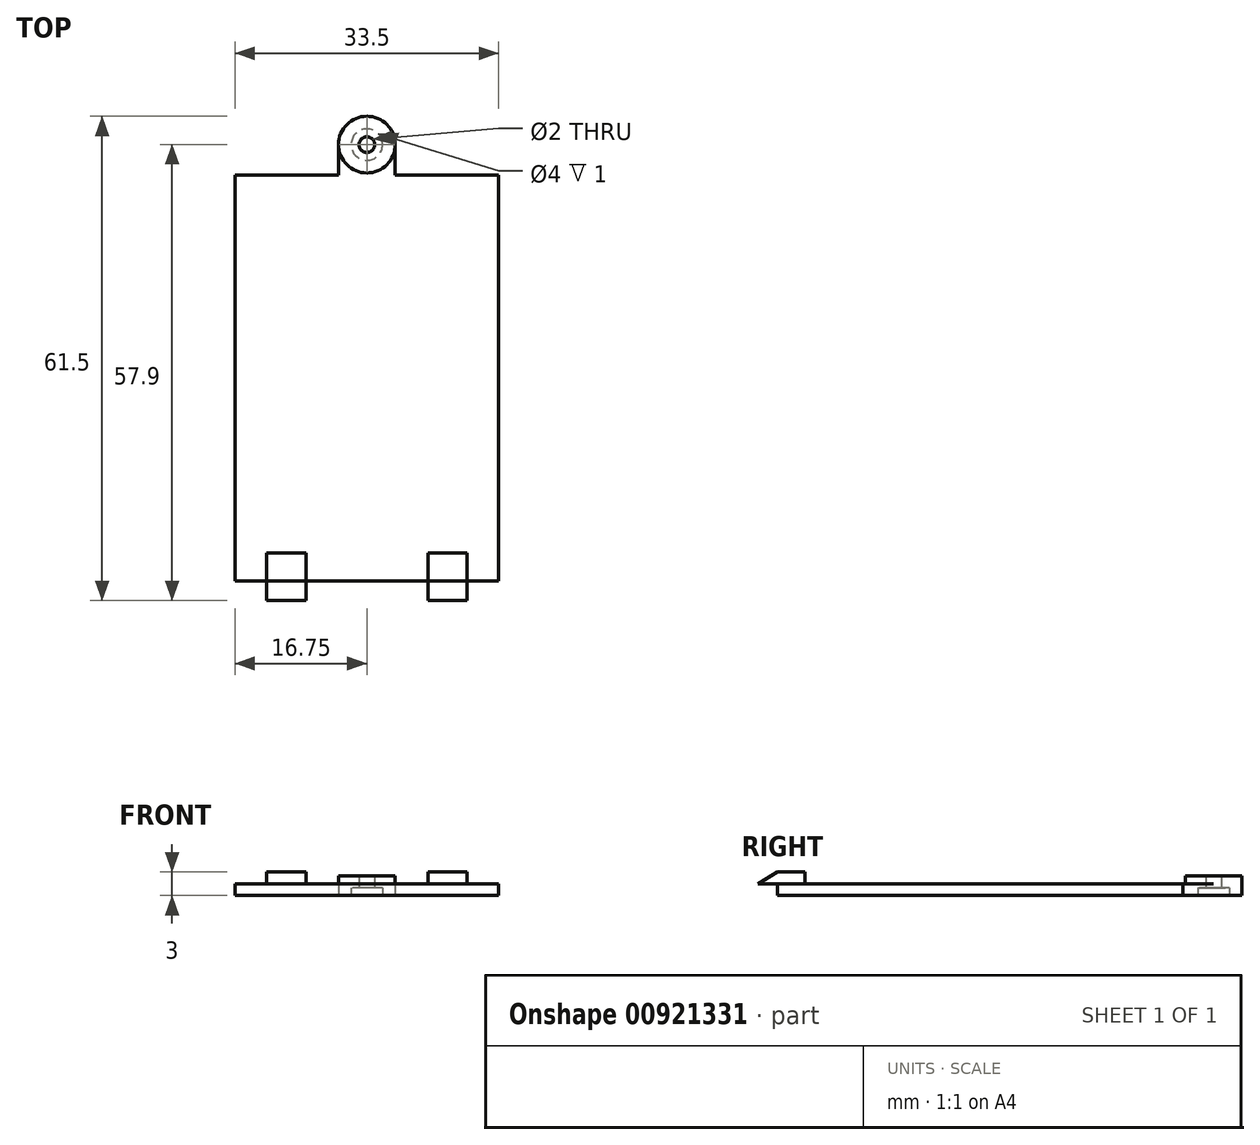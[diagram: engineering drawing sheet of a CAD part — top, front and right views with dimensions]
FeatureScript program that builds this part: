
annotation { "Feature Type Name" : "Feature", "Feature Type Description" : "" }
export const myFeature = defineFeature(function(context is Context, id is Id, definition is map)
    precondition{}
    {
        {
            var Q0;
            Q0=qCreatedBy(makeId("Top.planeOp"),FACE);
            var sketch = newSketch(context, id + "F0", { "sketchPlane" : qUnion([Q0])});
            skLineSegment(sketch, "E0", {"start": v(0, 0) * mm, "end": v(-16.75, 0) * mm});
            skLineSegment(sketch, "E1", {"start": v(0, 0) * mm, "end": v(16.75, 0) * mm});
            skLineSegment(sketch, "E2", {"start": v(16.75, 0) * mm, "end": v(16.75, 51.5) * mm});
            skLineSegment(sketch, "E3", {"start": v(16.75, 51.5) * mm, "end": v(-16.75, 51.5) * mm});
            skLineSegment(sketch, "E4", {"start": v(-16.75, 51.5) * mm, "end": v(-16.75, 0) * mm});
            skLineSegment(sketch, "E5", {"start": v(0, 51.5) * mm, "end": v(-3.6, 51.5) * mm});
            skCircle(sketch, "E6", {"center": v(0, 55.4) * mm, "radius": 3.6 * mm});
            skLineSegment(sketch, "E7", {"start": v(-3.6, 55.4) * mm, "end": v(-3.6, 51.5) * mm});
            skLineSegment(sketch, "E8", {"start": v(3.6, 55.4) * mm, "end": v(3.6, 51.5) * mm});
            skCircle(sketch, "E9", {"center": v(0, 55.4) * mm, "radius": 1 * mm});
            skCircle(sketch, "E10", {"center": v(0, 55.4) * mm, "radius": 2 * mm});
            skSolve(sketch);
        }
        {
            var Q0;
            Q0=makeQuery(id+"F0.imprint","IMPRINT",FACE,{"disambiguationData":[TD([[makeQuery(id+"F0.imprint","IMPRINT",EDGE,{"derivedFrom":sQuery(id+"F0.wireOp",EDGE,"E0")}),-1.0]])]});
            var Q1;
            {var subQ0=sQuery(id+"F0.wireOp",EDGE,"E5");Q1=makeQuery(id+"F0.imprint","IMPRINT",FACE,{"disambiguationData":[TD([[makeQuery(id+"F0.imprint","IMPRINT",EDGE,{"derivedFrom":subQ0}),-1.0]])]});}
            var Q2;
            {var subQ3=sQuery(id+"F0.wireOp",EDGE,"E8");Q2=makeQuery(id+"F0.imprint","IMPRINT",FACE,{"disambiguationData":[TD([[makeQuery(id+"F0.imprint","IMPRINT",EDGE,{"derivedFrom":subQ3}),-1.0]])]});}
            var Q3;
            {var subQ0=sQuery(id+"F0.wireOp",EDGE,"Crr1LPVL-UAtX-yI9U-8Ite-RvZtyMZe4BYH");Q3=makeQuery(id+"F0.imprint","IMPRINT",FACE,{"disambiguationData":[TD([[makeQuery(id+"F0.imprint","IMPRINT",EDGE,{"derivedFrom":subQ0}),-1.0]])]});}
            var Q4;
            {var subQ0=sQuery(id+"F0.wireOp",EDGE,"1Us7f2dU-Pjqd-qusr-gRFw-1HQ45FjS2ouL");Q4=makeQuery(id+"F0.imprint","IMPRINT",FACE,{"disambiguationData":[TD([[makeQuery(id+"F0.imprint","IMPRINT",EDGE,{"derivedFrom":subQ0}),1.0]])]});}
            var Q5;
            {var subQ0=sQuery(id+"F0.wireOp",EDGE,"3M23ZBgI-908c-eMXX-ZKFW-ISIKOpE3Sat9");Q5=makeQuery(id+"F0.imprint","IMPRINT",FACE,{"disambiguationData":[TD([[makeQuery(id+"F0.imprint","IMPRINT",EDGE,{"derivedFrom":subQ0}),-1.0]])]});}
            var Q6;
            {var subQ0=sQuery(id+"F0.wireOp",EDGE,"3M23ZBgI-908c-eMXX-ZKFW-ISIKOpE3Sat9");Q6=makeQuery(id+"F0.imprint","IMPRINT",FACE,{"disambiguationData":[TD([[makeQuery(id+"F0.imprint","IMPRINT",EDGE,{"derivedFrom":subQ0}),1.0]])]});}
            var Q7;
            Q7=makeQuery(id+"F0.imprint","IMPRINT",FACE,{"disambiguationData":[TD([[makeQuery(id+"F0.imprint","IMPRINT",EDGE,{"derivedFrom":sQuery(id+"F0.wireOp",EDGE,"E9")}),-1.0]])]});
            var Q8;
            Q8=makeQuery(id+"F0.imprint","IMPRINT",FACE,{"disambiguationData":[TD([[makeQuery(id+"F0.imprint","IMPRINT",EDGE,{"derivedFrom":sQuery(id+"F0.wireOp",EDGE,"E9")}),1.0]])]});
            var Q9;
            Q9=makeQuery(id+"F0.imprint","IMPRINT",FACE,{"disambiguationData":[TD([[makeQuery(id+"F0.imprint","IMPRINT",EDGE,{"derivedFrom":sQuery(id+"F0.wireOp",EDGE,"E10")}),-1.0]])]});
            extrude(context, id + "F1", {"entities" : qUnion([Q0, Q1, Q2, Q3, Q4, Q5, Q6, Q7, Q8, Q9]), "depth" : 1.5 * mm, "offsetDistance" : 25 * mm});
        }
        {
            var Q0;
            {var subQ0=sQuery(id+"F0.wireOp",EDGE,"Crr1LPVL-UAtX-yI9U-8Ite-RvZtyMZe4BYH");Q0=makeQuery(id+"F0.imprint","IMPRINT",FACE,{"disambiguationData":[TD([[makeQuery(id+"F0.imprint","IMPRINT",EDGE,{"derivedFrom":subQ0}),-1.0]])]});}
            var Q1;
            {var subQ0=sQuery(id+"F0.wireOp",EDGE,"1Us7f2dU-Pjqd-qusr-gRFw-1HQ45FjS2ouL");Q1=makeQuery(id+"F0.imprint","IMPRINT",FACE,{"disambiguationData":[TD([[makeQuery(id+"F0.imprint","IMPRINT",EDGE,{"derivedFrom":subQ0}),1.0]])]});}
            var Q2;
            {var subQ0=sQuery(id+"F0.wireOp",EDGE,"3M23ZBgI-908c-eMXX-ZKFW-ISIKOpE3Sat9");Q2=makeQuery(id+"F0.imprint","IMPRINT",FACE,{"disambiguationData":[TD([[makeQuery(id+"F0.imprint","IMPRINT",EDGE,{"derivedFrom":subQ0}),-1.0]])]});}
            var Q3;
            {var subQ0=sQuery(id+"F0.wireOp",EDGE,"3M23ZBgI-908c-eMXX-ZKFW-ISIKOpE3Sat9");Q3=makeQuery(id+"F0.imprint","IMPRINT",FACE,{"disambiguationData":[TD([[makeQuery(id+"F0.imprint","IMPRINT",EDGE,{"derivedFrom":subQ0}),1.0]])]});}
            var Q4;
            {var subQ0=sQuery(id+"F0.wireOp",EDGE,"E6");var subQ1=makeQuery(id+"F0.imprint","INTERSECT",VERTEX,{"derivedFrom":[subQ0,sQuery(id+"F0.wireOp",EDGE,"E7")]});Q4=makeQuery(id+"F0.imprint","IMPRINT",FACE,{"disambiguationData":[TD([[makeQuery(id+"F0.imprint","IMPRINT",EDGE,{"disambiguationData":[TD([[subQ1,1.0]])],"derivedFrom":subQ0}),1.0]])]});}
            var Q5;
            Q5=makeQuery(id+"F0.imprint","IMPRINT",FACE,{"disambiguationData":[TD([[makeQuery(id+"F0.imprint","IMPRINT",EDGE,{"derivedFrom":sQuery(id+"F0.wireOp",EDGE,"E9")}),-1.0]])]});
            var Q6;
            Q6=makeQuery(id+"F0.imprint","IMPRINT",FACE,{"disambiguationData":[TD([[makeQuery(id+"F0.imprint","IMPRINT",EDGE,{"derivedFrom":sQuery(id+"F0.wireOp",EDGE,"E9")}),1.0]])]});
            extrude(context, id + "F2", {"entities" : qUnion([Q0, Q1, Q2, Q3, Q4, Q5, Q6]), "operationType" : NewBodyOperationType.ADD, "depth" : 2.5 * mm, "offsetDistance" : 25 * mm});
        }
        {
            var Q0;
            Q0=makeQuery(id+"F1.opExtrude","CAP_FACE",FACE,{"disambiguationData":[OSD([sQuery(id+"F0.wireOp",EDGE,"E0"),sQuery(id+"F0.wireOp",EDGE,"E1"),sQuery(id+"F0.wireOp",EDGE,"E2"),sQuery(id+"F0.wireOp",EDGE,"E3"),sQuery(id+"F0.wireOp",EDGE,"E4"),sQuery(id+"F0.wireOp",EDGE,"E6"),sQuery(id+"F0.wireOp",EDGE,"E7"),sQuery(id+"F0.wireOp",EDGE,"E8")])],"isStart":false});
            var sketch = newSketch(context, id + "F3", { "sketchPlane" : qUnion([Q0])});
            skLineSegment(sketch, "E11", {"start": v(12.74, 0) * mm, "end": v(12.74, 3.5) * mm});
            skLineSegment(sketch, "E12", {"start": v(12.74, 3.5) * mm, "end": v(7.74, 3.5) * mm});
            skLineSegment(sketch, "E13", {"start": v(7.74, 3.5) * mm, "end": v(7.74, -2.5) * mm});
            skLineSegment(sketch, "E14", {"start": v(7.74, -2.5) * mm, "end": v(12.74, -2.5) * mm});
            skLineSegment(sketch, "E15", {"start": v(12.74, -2.5) * mm, "end": v(12.74, 0) * mm});
            skLineSegment(sketch, "E16", {"start": v(0, 0.9) * mm, "end": v(0, 19.62) * mm});
            skLineSegment(sketch, "E17.MirrorCS", {"start": v(-12.74, 3.5) * mm, "end": v(-7.74, 3.5) * mm});
            skLineSegment(sketch, "E18.MirrorCS", {"start": v(-12.74, 0) * mm, "end": v(-12.74, 3.5) * mm});
            skLineSegment(sketch, "E19.MirrorCS", {"start": v(-12.74, -2.5) * mm, "end": v(-12.74, 0) * mm});
            skLineSegment(sketch, "E20.MirrorCS", {"start": v(-7.74, -2.5) * mm, "end": v(-12.74, -2.5) * mm});
            skLineSegment(sketch, "E21.MirrorCS", {"start": v(-7.74, 3.5) * mm, "end": v(-7.74, -2.5) * mm});
            skSolve(sketch);
        }
        {
            var Q0;
            {var subQ0=sQuery(id+"F3.wireOp",EDGE,"E19.MirrorCS");Q0=makeQuery(id+"F3.imprint","IMPRINT",FACE,{"disambiguationData":[TD([[makeQuery(id+"F3.imprint","IMPRINT",EDGE,{"derivedFrom":subQ0}),-1.0]])]});}
            var Q1;
            {var subQ0=sQuery(id+"F3.wireOp",EDGE,"E17.MirrorCS");Q1=makeQuery(id+"F3.imprint","IMPRINT",FACE,{"disambiguationData":[TD([[makeQuery(id+"F3.imprint","IMPRINT",EDGE,{"derivedFrom":subQ0}),-1.0]])]});}
            var Q2;
            {var subQ0=sQuery(id+"F3.wireOp",EDGE,"E14");Q2=makeQuery(id+"F3.imprint","IMPRINT",FACE,{"disambiguationData":[TD([[makeQuery(id+"F3.imprint","IMPRINT",EDGE,{"derivedFrom":subQ0}),1.0]])]});}
            var Q3;
            {var subQ0=sQuery(id+"F3.wireOp",EDGE,"E11");Q3=makeQuery(id+"F3.imprint","IMPRINT",FACE,{"disambiguationData":[TD([[makeQuery(id+"F3.imprint","IMPRINT",EDGE,{"derivedFrom":subQ0}),1.0]])]});}
            extrude(context, id + "F4", {"entities" : qUnion([Q0, Q1, Q2, Q3]), "operationType" : NewBodyOperationType.ADD, "depth" : 1.5 * mm, "offsetDistance" : 25 * mm});
        }
        {
            var Q0;
            Q0=makeQuery(id+"F4.opExtrude","CAP_EDGE",EDGE,{"disambiguationData":[OSD([sQuery(id+"F3.wireOp",EDGE,"E20.MirrorCS")])],"isStart":false});
            chamfer(context, id + "F5", {"entities" : qUnion([Q0]), "chamferType" : ChamferType.TWO_OFFSETS, "width1" : 1.5 * mm, "oppositeDirection" : false, "width2" : 2.5 * mm, "tangentPropagation" : true});
        }
        {
            var Q0;
            Q0=makeQuery(id+"F4.opExtrude","CAP_EDGE",EDGE,{"disambiguationData":[OSD([sQuery(id+"F3.wireOp",EDGE,"E14")])],"isStart":false});
            chamfer(context, id + "F6", {"entities" : qUnion([Q0]), "chamferType" : ChamferType.TWO_OFFSETS, "width1" : 2.5 * mm, "oppositeDirection" : false, "width2" : 1.5 * mm, "tangentPropagation" : true});
        }
        {
            var Q0;
            Q0=makeQuery(id+"F0.imprint","IMPRINT",FACE,{"disambiguationData":[TD([[makeQuery(id+"F0.imprint","IMPRINT",EDGE,{"derivedFrom":sQuery(id+"F0.wireOp",EDGE,"E9")}),1.0]])]});
            extrude(context, id + "F7", {"entities" : qUnion([Q0]), "operationType" : NewBodyOperationType.REMOVE, "oppositeDirection" : true, "depth" : -25 * mm, "offsetDistance" : 25 * mm});
        }
        {
            var Q0;
            Q0=makeQuery(id+"F0.imprint","IMPRINT",FACE,{"disambiguationData":[TD([[makeQuery(id+"F0.imprint","IMPRINT",EDGE,{"derivedFrom":sQuery(id+"F0.wireOp",EDGE,"E9")}),-1.0]])]});
            extrude(context, id + "F8", {"entities" : qUnion([Q0]), "operationType" : NewBodyOperationType.REMOVE, "oppositeDirection" : true, "depth" : -1 * mm, "offsetDistance" : 25 * mm});
        }
    });
